# Revit family: TY6236
name_source: partatom
category: Sprinklers
revit_build: Autodesk Revit 2016 (Build: 20150220_1215(x64)
units: mm (PartAtom-declared; Revit-internal decimal feet)

## family parameters
Always vertical = Yes
Cut with Voids When Loaded = No
Maintain Annotation Orientation = No
OmniClass Number = 23.65.70.17.11.24
OmniClass Title = Fire Fighting Sprinkler Heads
Part Type = Normal
Room Calculation Point = No
Round Connector Dimension = Use Diameter
Shared = No
Work Plane-Based = No

## types (4) — shared parameters
COBie = Yes
COBie.Component.Name = Sprinklers:ESFR Upright_SIN
COBie.Type = Yes
COBie.Type.AssetType = Fixed
COBie.Type.Category = Pr_70_55_97_84:Sprinklers
COBie.Type.Colour = Yellow
COBie.Type.DurationUnit = year
COBie.Type.Finish = Natural Brass
COBie.Type.Manufacturer = Tyco Fire Protection Products
COBie.Type.Material = Brass
COBie.Type.Shape = Cylinder
COBie.Type.Size = 3/4"(DN20)
COBie.Type.WarrantyGuarantorParts = http://tycofsbp.com
TFPPTerms_of_Sale.pdf
Coverage = Standard
K-Factor = 199.7739
Manufacturer = Tyco Fire Protection Products
Manufacturer URL = www.tyco-fire.com
Model = ESFR-14
Nominal Diameter 1 = 20 mm
Orifice = Extra Large
Orifice Size = 20 mm
Outside Diameter 1 = 27 mm
Response = Quick
SIN No = TY6236
Takeout 1 = 60 mm
Technical Data Sheet No = TFP319
zero-valued in all types: COBie.Type.NominalHeight, COBie.Type.NominalLength, COBie.Type.NominalWidth, COBie.Type.ReplacementCost, Style Id

## per-type parameters (varying)
| type | COBie.Component.Description | COBie.Component.InstallationDate | COBie.Type.ModelNumber | COBie.Type.ModelReference | Part No | Temperature Rating |
| ESFR-14 ESFR Pendent Brass 155°F/68°C 14K ¾" ISO_58-443-1-155 | ESFR-14 Wet ESFR Pendent  68.3°C K200 DN20 ISO Br |  | 58-443-1-155 | ESFR-14 Wet ESFR Pendent  68.3°C K200 DN20 ISO Br | 58-443-1-155 | 68 °C |
| ESFR-14 ESFR Pendent Brass 200°F/93°C 14K ¾" ISO_58-443-1-200 | ESFR-14 Wet ESFR Pendent  93.3°C K200 DN20 ISO Br | 1900-12-31T23:59:59 | 58-443-1-200 | ESFR-14 Wet ESFR Pendent  93.3°C K200 DN20 ISO Br | 58-443-1-200 | 93 °C |
| ESFR-14 ESFR Pendent Brass 155°F/68°C 14K ¾" NPT_58-449-1-155 | ESFR-14 Wet ESFR Pendent  68.3°C K200 DN20 NPT Br |  | 58-449-1-155 | ESFR-14 Wet ESFR Pendent  68.3°C K200 DN20 NPT Br | 58-449-1-155 | 68 °C |
| ESFR-14 ESFR Pendent Brass 200°F/93°C 14K ¾" NPT_58-449-1-200 | ESFR-14 Wet ESFR Pendent  93.3°C K200 DN20 NPT Br |  | 58-449-1-200 | ESFR-14 Wet ESFR Pendent  93.3°C K200 DN20 NPT Br | 58-449-1-200 | 93 °C |

note: column(s) folded — value = type name in every type: Description

## geometry (parser evidence)
native form markers: Blend x2, Sweep x70
no freeform markers — native parametric forms only
